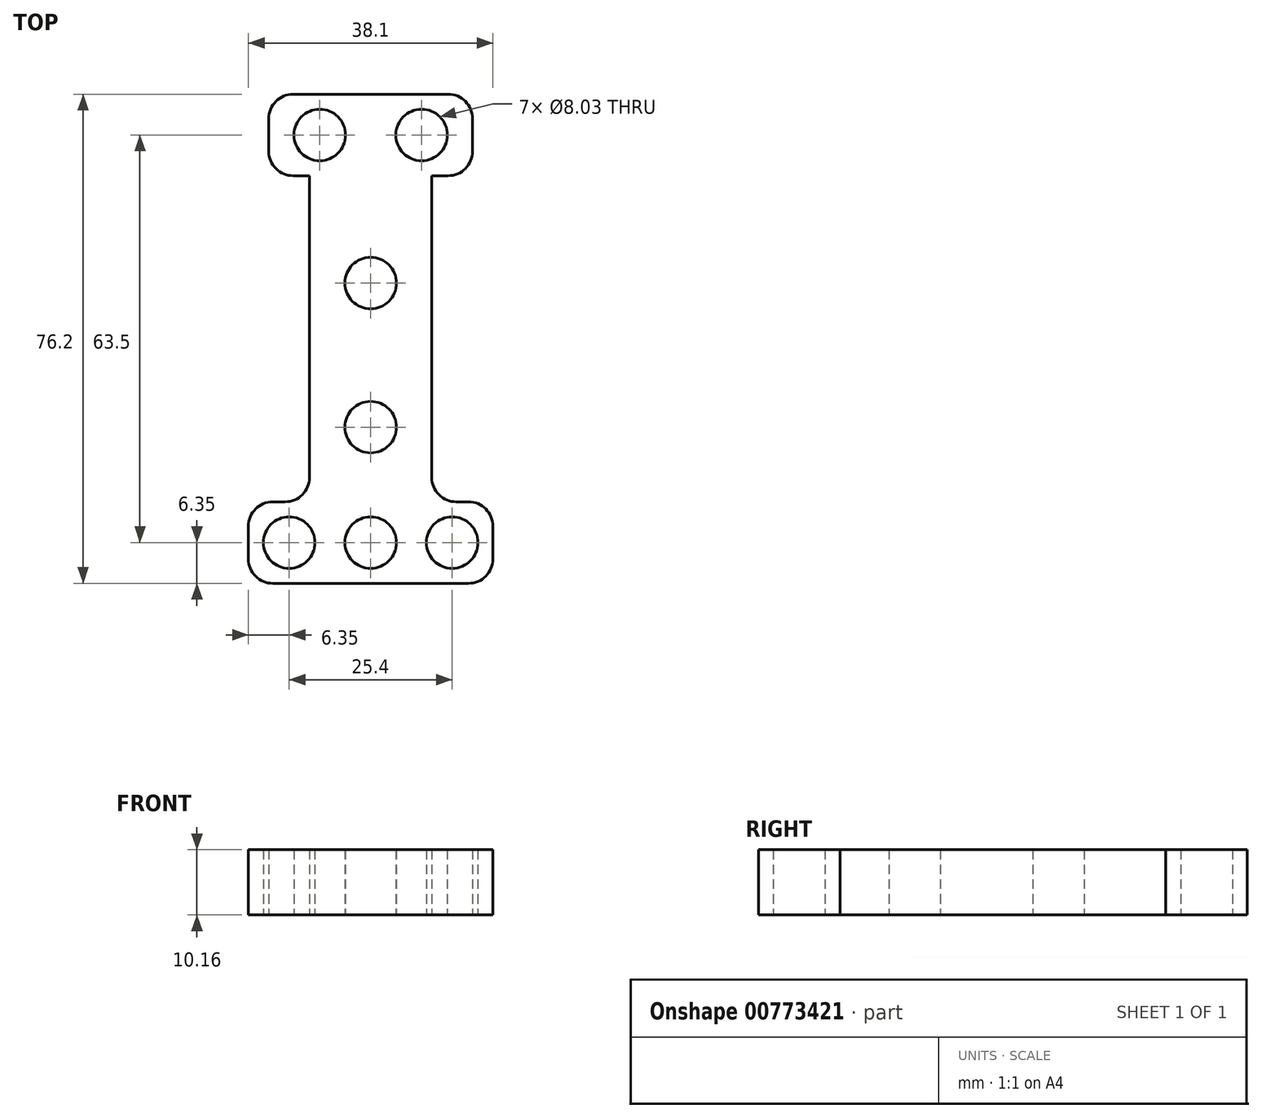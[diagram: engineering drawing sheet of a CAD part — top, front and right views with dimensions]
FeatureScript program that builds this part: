
annotation { "Feature Type Name" : "Feature", "Feature Type Description" : "" }
export const myFeature = defineFeature(function(context is Context, id is Id, definition is map)
    precondition{}
    {
        {
            var Q0;
            Q0=qCreatedBy(makeId("Top.planeOp"),FACE);
            var sketch = newSketch(context, id + "F0", { "sketchPlane" : qUnion([Q0])});
            skLineSegment(sketch, "E0.bottom", {"start": v(19.05, -6.35) * mm, "end": v(-19.05, -6.35) * mm});
            skLineSegment(sketch, "E0.top", {"start": v(19.05, 6.35) * mm, "end": v(-19.05, 6.35) * mm});
            skLineSegment(sketch, "E0.left", {"start": v(19.05, -6.35) * mm, "end": v(19.05, 6.35) * mm});
            skLineSegment(sketch, "E0.right", {"start": v(-19.05, -6.35) * mm, "end": v(-19.05, 6.35) * mm});
            skPoint(sketch, "E0.middle", {"position": v(0, 0) * mm});
            skLineSegment(sketch, "E1.bottom", {"start": v(-9.52, 6.35) * mm, "end": v(9.53, 6.35) * mm});
            skLineSegment(sketch, "E1.top", {"start": v(-9.53, 69.85) * mm, "end": v(9.52, 69.85) * mm});
            skLineSegment(sketch, "E1.left", {"start": v(-9.52, 6.35) * mm, "end": v(-9.53, 69.85) * mm});
            skLineSegment(sketch, "E1.right", {"start": v(9.53, 6.35) * mm, "end": v(9.52, 69.85) * mm});
            skCircle(sketch, "E2", {"center": v(-12.7, 0) * mm, "radius": 4.01 * mm});
            skCircle(sketch, "E3", {"center": v(0, 0) * mm, "radius": 4.01 * mm});
            skCircle(sketch, "E4", {"center": v(12.7, 0) * mm, "radius": 4.01 * mm});
            skSolve(sketch);
        }
        {
            var Q0;
            Q0=makeQuery(id+"F0.imprint","IMPRINT",FACE,{"disambiguationData":[TD([[makeQuery(id+"F0.imprint","IMPRINT",EDGE,{"derivedFrom":sQuery(id+"F0.wireOp",EDGE,"E1.top")}),-1.0]])]});
            var Q1;
            Q1=makeQuery(id+"F0.imprint","IMPRINT",FACE,{"disambiguationData":[TD([[makeQuery(id+"F0.imprint","IMPRINT",EDGE,{"derivedFrom":sQuery(id+"F0.wireOp",EDGE,"E0.bottom")}),-1.0]])]});
            extrude(context, id + "F1", {"entities" : qUnion([Q0, Q1]), "depth" : 10.16 * mm});
        }
        {
            var Q0;
            Q0=makeQuery(id+"F1.opExtrude","CAP_FACE",FACE,{"disambiguationData":[OSD([sQuery(id+"F0.wireOp",EDGE,"E0.bottom"),sQuery(id+"F0.wireOp",EDGE,"E0.top"),sQuery(id+"F0.wireOp",EDGE,"E0.left"),sQuery(id+"F0.wireOp",EDGE,"E0.right"),sQuery(id+"F0.wireOp",EDGE,"E1.top"),sQuery(id+"F0.wireOp",EDGE,"E1.left"),sQuery(id+"F0.wireOp",EDGE,"E1.right"),sQuery(id+"F0.wireOp",EDGE,"E2"),sQuery(id+"F0.wireOp",EDGE,"E3"),sQuery(id+"F0.wireOp",EDGE,"E4")])],"isStart":true});
            var sketch = newSketch(context, id + "F2", { "sketchPlane" : qUnion([Q0])});
            skCircle(sketch, "E5", {"center": v(0, -17.98) * mm, "radius": 4.01 * mm});
            skSolve(sketch);
        }
        {
            var Q0;
            Q0=makeQuery(id+"F2.imprint","IMPRINT",FACE,{"disambiguationData":[TD([[makeQuery(id+"F2.imprint","IMPRINT",EDGE,{"derivedFrom":sQuery(id+"F2.wireOp",EDGE,"E5")}),1.0]])]});
            extrude(context, id + "F3", {"entities" : qUnion([Q0]), "operationType" : NewBodyOperationType.REMOVE, "oppositeDirection" : true, "depth" : 25.4 * mm});
        }
        {
            var Q0;
            Q0=makeQuery(id+"F1.opExtrude","CAP_FACE",FACE,{"disambiguationData":[OSD([sQuery(id+"F0.wireOp",EDGE,"E0.bottom"),sQuery(id+"F0.wireOp",EDGE,"E0.top"),sQuery(id+"F0.wireOp",EDGE,"E0.left"),sQuery(id+"F0.wireOp",EDGE,"E0.right"),sQuery(id+"F0.wireOp",EDGE,"E1.top"),sQuery(id+"F0.wireOp",EDGE,"E1.left"),sQuery(id+"F0.wireOp",EDGE,"E1.right"),sQuery(id+"F0.wireOp",EDGE,"E2"),sQuery(id+"F0.wireOp",EDGE,"E3"),sQuery(id+"F0.wireOp",EDGE,"E4")])],"isStart":true});
            var sketch = newSketch(context, id + "F4", { "sketchPlane" : qUnion([Q0])});
            skLineSegment(sketch, "E6.bottom", {"start": v(-9.53, -69.85) * mm, "end": v(-15.88, -69.85) * mm});
            skLineSegment(sketch, "E6.top", {"start": v(-9.53, -57.15) * mm, "end": v(-15.88, -57.15) * mm});
            skLineSegment(sketch, "E6.left", {"start": v(-9.53, -69.85) * mm, "end": v(-9.53, -57.15) * mm});
            skLineSegment(sketch, "E6.right", {"start": v(-15.87, -69.85) * mm, "end": v(-15.88, -57.15) * mm});
            skLineSegment(sketch, "E7.bottom", {"start": v(9.52, -69.85) * mm, "end": v(15.87, -69.85) * mm});
            skLineSegment(sketch, "E7.top", {"start": v(9.52, -57.15) * mm, "end": v(15.87, -57.15) * mm});
            skLineSegment(sketch, "E7.left", {"start": v(9.52, -69.85) * mm, "end": v(9.52, -57.15) * mm});
            skLineSegment(sketch, "E7.right", {"start": v(15.88, -69.85) * mm, "end": v(15.88, -57.15) * mm});
            skSolve(sketch);
        }
        {
            var Q0;
            Q0=makeQuery(id+"F4.imprint","IMPRINT",FACE,{"disambiguationData":[TD([[makeQuery(id+"F4.imprint","IMPRINT",EDGE,{"derivedFrom":sQuery(id+"F4.wireOp",EDGE,"E6.bottom")}),-1.0]])]});
            var Q1;
            Q1=makeQuery(id+"F4.imprint","IMPRINT",FACE,{"disambiguationData":[TD([[makeQuery(id+"F4.imprint","IMPRINT",EDGE,{"derivedFrom":sQuery(id+"F4.wireOp",EDGE,"E7.bottom")}),1.0]])]});
            extrude(context, id + "F5", {"entities" : qUnion([Q0, Q1]), "operationType" : NewBodyOperationType.ADD, "oppositeDirection" : true, "depth" : 10.16 * mm});
        }
        {
            var Q0;
            Q0=makeQuery(id+"F5.boolean.opBoolean","MERGE",FACE,{"derivedFrom":[makeQuery(id+"F1.opExtrude","CAP_FACE",FACE,{"disambiguationData":[OSD([sQuery(id+"F0.wireOp",EDGE,"E0.bottom"),sQuery(id+"F0.wireOp",EDGE,"E0.top"),sQuery(id+"F0.wireOp",EDGE,"E0.left"),sQuery(id+"F0.wireOp",EDGE,"E0.right"),sQuery(id+"F0.wireOp",EDGE,"E1.top"),sQuery(id+"F0.wireOp",EDGE,"E1.left"),sQuery(id+"F0.wireOp",EDGE,"E1.right"),sQuery(id+"F0.wireOp",EDGE,"E2"),sQuery(id+"F0.wireOp",EDGE,"E3"),sQuery(id+"F0.wireOp",EDGE,"E4")])],"isStart":true}),makeQuery(id+"F5.opExtrude","CAP_FACE",FACE,{"disambiguationData":[OSD([sQuery(id+"F4.wireOp",EDGE,"E6.bottom"),sQuery(id+"F4.wireOp",EDGE,"E6.top"),sQuery(id+"F4.wireOp",EDGE,"E6.left"),sQuery(id+"F4.wireOp",EDGE,"E6.right")])],"isStart":true}),makeQuery(id+"F5.opExtrude","CAP_FACE",FACE,{"disambiguationData":[OSD([sQuery(id+"F4.wireOp",EDGE,"E7.bottom"),sQuery(id+"F4.wireOp",EDGE,"E7.top"),sQuery(id+"F4.wireOp",EDGE,"E7.left"),sQuery(id+"F4.wireOp",EDGE,"E7.right")])],"isStart":true})]});
            var sketch = newSketch(context, id + "F6", { "sketchPlane" : qUnion([Q0])});
            skCircle(sketch, "E8", {"center": v(7.94, -63.5) * mm, "radius": 4.01 * mm});
            skCircle(sketch, "E9", {"center": v(-7.94, -63.5) * mm, "radius": 4.01 * mm});
            skLineSegment(sketch, "E10", {"start": v(-15.87, -63.5) * mm, "end": v(15.88, -63.5) * mm});
            skSolve(sketch);
        }
        {
            var Q0;
            {var subQ0=sQuery(id+"F6.wireOp",EDGE,"E10");var subQ1=sQuery(id+"F6.wireOp",EDGE,"E9");var subQ2=makeQuery(id+"F6.imprint","INTERSECT",VERTEX,{"disambiguationData":[OD(0.0)],"derivedFrom":[subQ1,subQ0]});Q0=makeQuery(id+"F6.imprint","IMPRINT",FACE,{"disambiguationData":[TD([[makeQuery(id+"F6.imprint","IMPRINT",EDGE,{"disambiguationData":[TD([[subQ2,1.0]])],"derivedFrom":subQ1}),1.0]])]});}
            var Q1;
            {var subQ0=sQuery(id+"F6.wireOp",EDGE,"E10");var subQ1=sQuery(id+"F6.wireOp",EDGE,"E9");var subQ2=makeQuery(id+"F6.imprint","INTERSECT",VERTEX,{"disambiguationData":[OD(0.0)],"derivedFrom":[subQ1,subQ0]});Q1=makeQuery(id+"F6.imprint","IMPRINT",FACE,{"disambiguationData":[TD([[makeQuery(id+"F6.imprint","IMPRINT",EDGE,{"disambiguationData":[TD([[subQ2,-1.0]])],"derivedFrom":subQ1}),1.0]])]});}
            var Q2;
            {var subQ0=sQuery(id+"F6.wireOp",EDGE,"E10");var subQ1=sQuery(id+"F6.wireOp",EDGE,"E8");var subQ2=makeQuery(id+"F6.imprint","INTERSECT",VERTEX,{"disambiguationData":[OD(0.0)],"derivedFrom":[subQ1,subQ0]});Q2=makeQuery(id+"F6.imprint","IMPRINT",FACE,{"disambiguationData":[TD([[makeQuery(id+"F6.imprint","IMPRINT",EDGE,{"disambiguationData":[TD([[subQ2,-1.0]])],"derivedFrom":subQ1}),1.0]])]});}
            var Q3;
            {var subQ0=sQuery(id+"F6.wireOp",EDGE,"E10");var subQ1=sQuery(id+"F6.wireOp",EDGE,"E8");var subQ2=makeQuery(id+"F6.imprint","INTERSECT",VERTEX,{"disambiguationData":[OD(0.0)],"derivedFrom":[subQ1,subQ0]});Q3=makeQuery(id+"F6.imprint","IMPRINT",FACE,{"disambiguationData":[TD([[makeQuery(id+"F6.imprint","IMPRINT",EDGE,{"disambiguationData":[TD([[subQ2,1.0]])],"derivedFrom":subQ1}),1.0]])]});}
            extrude(context, id + "F7", {"entities" : qUnion([Q0, Q1, Q2, Q3]), "operationType" : NewBodyOperationType.REMOVE, "oppositeDirection" : true, "depth" : 25.4 * mm});
        }
        {
            var Q0;
            Q0=makeQuery(id+"F1.opExtrude","SWEPT_EDGE",EDGE,{"disambiguationData":[OSD([sQuery(id+"F0.wireOp",EDGE,"E0.bottom"),sQuery(id+"F0.wireOp",EDGE,"E0.left")])]});
            var Q1;
            Q1=makeQuery(id+"F1.opExtrude","SWEPT_EDGE",EDGE,{"disambiguationData":[OSD([sQuery(id+"F0.wireOp",EDGE,"E0.bottom"),sQuery(id+"F0.wireOp",EDGE,"E0.right")])]});
            var Q2;
            Q2=makeQuery(id+"F1.opExtrude","SWEPT_EDGE",EDGE,{"disambiguationData":[OSD([sQuery(id+"F0.wireOp",EDGE,"E0.top"),sQuery(id+"F0.wireOp",EDGE,"E0.right")])]});
            var Q3;
            Q3=makeQuery(id+"F1.opExtrude","SWEPT_EDGE",EDGE,{"disambiguationData":[OSD([sQuery(id+"F0.wireOp",EDGE,"E0.top"),sQuery(id+"F0.wireOp",EDGE,"E0.left")])]});
            var Q4;
            Q4=makeQuery(id+"F5.opExtrude","SWEPT_EDGE",EDGE,{"disambiguationData":[OSD([sQuery(id+"F4.wireOp",EDGE,"E7.top"),sQuery(id+"F4.wireOp",EDGE,"E7.right")])]});
            var Q5;
            Q5=makeQuery(id+"F5.opExtrude","SWEPT_EDGE",EDGE,{"disambiguationData":[OSD([sQuery(id+"F4.wireOp",EDGE,"E7.bottom"),sQuery(id+"F4.wireOp",EDGE,"E7.right")])]});
            var Q6;
            Q6=makeQuery(id+"F5.opExtrude","SWEPT_EDGE",EDGE,{"disambiguationData":[OSD([sQuery(id+"F4.wireOp",EDGE,"E6.bottom"),sQuery(id+"F4.wireOp",EDGE,"E6.right")])]});
            var Q7;
            Q7=makeQuery(id+"F5.opExtrude","SWEPT_EDGE",EDGE,{"disambiguationData":[OSD([sQuery(id+"F4.wireOp",EDGE,"E6.top"),sQuery(id+"F4.wireOp",EDGE,"E6.right")])]});
            fillet(context, id + "F8", {"entities" : qUnion([Q0, Q1, Q2, Q3, Q4, Q5, Q6, Q7]), "radius" : 3.8 * mm, "tangentPropagation" : true, "allowEdgeOverflow" : false});
        }
        {
            var Q0;
            Q0=makeQuery(id+"F1.opExtrude","SWEPT_EDGE",EDGE,{"disambiguationData":[OSD([sQuery(id+"F0.wireOp",EDGE,"E0.top"),sQuery(id+"F0.wireOp",EDGE,"E1.left")])]});
            var Q1;
            Q1=makeQuery(id+"F5.opExtrude","SWEPT_EDGE",EDGE,{"disambiguationData":[OSD([sQuery(id+"F0.wireOp",EDGE,"E1.left"),sQuery(id+"F4.wireOp",EDGE,"E6.top"),sQuery(id+"F4.wireOp",EDGE,"E6.left")])]});
            var Q2;
            Q2=makeQuery(id+"F1.opExtrude","SWEPT_EDGE",EDGE,{"disambiguationData":[OSD([sQuery(id+"F0.wireOp",EDGE,"E0.top"),sQuery(id+"F0.wireOp",EDGE,"E1.right")])]});
            var Q3;
            Q3=makeQuery(id+"F5.opExtrude","SWEPT_EDGE",EDGE,{"disambiguationData":[OSD([sQuery(id+"F0.wireOp",EDGE,"E1.right"),sQuery(id+"F4.wireOp",EDGE,"E7.top"),sQuery(id+"F4.wireOp",EDGE,"E7.left")])]});
            fillet(context, id + "F9", {"entities" : qUnion([Q0, Q1, Q2, Q3]), "radius" : 3.8 * mm, "tangentPropagation" : true, "allowEdgeOverflow" : false});
        }
        {
            var Q0;
            Q0=makeQuery(id+"F5.boolean.opBoolean","MERGE",FACE,{"derivedFrom":[makeQuery(id+"F1.opExtrude","CAP_FACE",FACE,{"disambiguationData":[OSD([sQuery(id+"F0.wireOp",EDGE,"E0.bottom"),sQuery(id+"F0.wireOp",EDGE,"E0.top"),sQuery(id+"F0.wireOp",EDGE,"E0.left"),sQuery(id+"F0.wireOp",EDGE,"E0.right"),sQuery(id+"F0.wireOp",EDGE,"E1.top"),sQuery(id+"F0.wireOp",EDGE,"E1.left"),sQuery(id+"F0.wireOp",EDGE,"E1.right"),sQuery(id+"F0.wireOp",EDGE,"E2"),sQuery(id+"F0.wireOp",EDGE,"E3"),sQuery(id+"F0.wireOp",EDGE,"E4")])],"isStart":true}),makeQuery(id+"F5.opExtrude","CAP_FACE",FACE,{"disambiguationData":[OSD([sQuery(id+"F4.wireOp",EDGE,"E6.bottom"),sQuery(id+"F4.wireOp",EDGE,"E6.top"),sQuery(id+"F4.wireOp",EDGE,"E6.left"),sQuery(id+"F4.wireOp",EDGE,"E6.right")])],"isStart":true}),makeQuery(id+"F5.opExtrude","CAP_FACE",FACE,{"disambiguationData":[OSD([sQuery(id+"F4.wireOp",EDGE,"E7.bottom"),sQuery(id+"F4.wireOp",EDGE,"E7.top"),sQuery(id+"F4.wireOp",EDGE,"E7.left"),sQuery(id+"F4.wireOp",EDGE,"E7.right")])],"isStart":true})]});
            var sketch = newSketch(context, id + "F10", { "sketchPlane" : qUnion([Q0])});
            skCircle(sketch, "E11", {"center": v(0, -40.44) * mm, "radius": 4.01 * mm});
            skSolve(sketch);
        }
        {
            var Q0;
            Q0=makeQuery(id+"F10.imprint","IMPRINT",FACE,{"disambiguationData":[TD([[makeQuery(id+"F10.imprint","IMPRINT",EDGE,{"derivedFrom":sQuery(id+"F10.wireOp",EDGE,"E11")}),1.0]])]});
            extrude(context, id + "F11", {"entities" : qUnion([Q0]), "operationType" : NewBodyOperationType.REMOVE, "oppositeDirection" : true, "depth" : 25.4 * mm});
        }
    });
